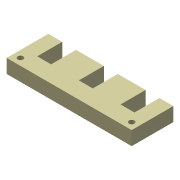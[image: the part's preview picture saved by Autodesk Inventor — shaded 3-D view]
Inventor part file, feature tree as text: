
AUTODESK INVENTOR PART (.ipt)
format: ipt  version: 2013 (Build 170138000, 138)  size: 139,776 bytes
history: native  units: in
note: dims shown in document units (in); Inventor stores cm internally (conversion verified against a paired STEP export)
features: extrude x3, sketch x3
ambient origin geometry x8: Origin, YZ Plane, XZ Plane, XY Plane, X Axis, Y Axis, Z Axis, Center Point
bodies: Solid1 (feature_tree)
feature tree (6):
  extrude  "Extrusion1"  Depth=1.1811in
  extrude  "Extrusion3"  Depth=0.7874in
  extrude  "Extrusion5"  Depth=0.7087in
  sketch  "Sketch1"  dims[d0=3.5433in d3=1.1811in]
  sketch  "Sketch2"  dims[d4=0.3937in d5=0.7874in]
  sketch  "Sketch4"  dims[d6=0.7874in d7=0.7087in d8=0.7087in d9=0.7087in d10=0.7087in d11=0.7087in d12=0.3937in d13=0.3937in d14=0.3937in d15=0.3937in d16=0.0in d17=0.7087in d18=1.1811in d20=0.1575in d22=0.1969in d23=0.1969in d26=0.1969in d27=0.1969in d29=0.1575in d32=0.3937in d33=0.0in d43=0.5906in d44=0.5906in d45=0.3937in d46=0.3937in d47=0.1575in d48=0.1575in d49=0.315in d50=0.0in]
